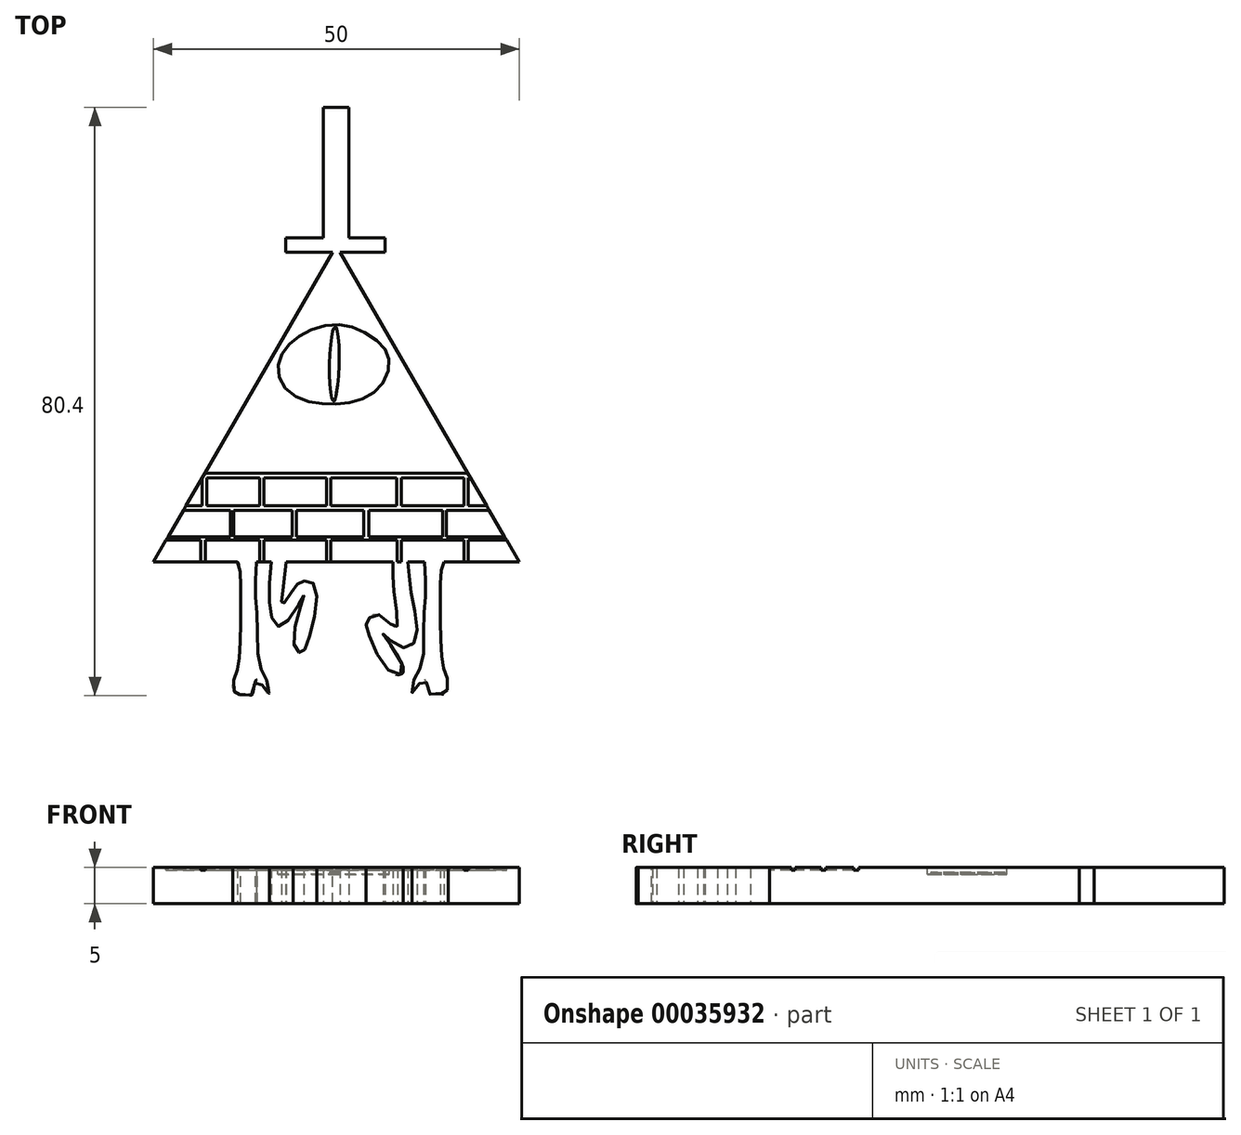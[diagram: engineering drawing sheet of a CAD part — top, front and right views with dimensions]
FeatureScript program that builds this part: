
annotation { "Feature Type Name" : "Feature", "Feature Type Description" : "" }
export const myFeature = defineFeature(function(context is Context, id is Id, definition is map)
    precondition{}
    {
        {
            var Q0;
            Q0=qCreatedBy(makeId("Top.planeOp"),FACE);
            var sketch = newSketch(context, id + "F0", { "sketchPlane" : qUnion([Q0])});
            skLineSegment(sketch, "E0", {"start": v(0, 43.3) * mm, "end": v(-25, 0) * mm});
            skLineSegment(sketch, "E1", {"start": v(-25, 0) * mm, "end": v(25, 0) * mm});
            skLineSegment(sketch, "E2", {"start": v(25, 0) * mm, "end": v(0, 43.3) * mm});
            skLineSegment(sketch, "E3.bottom", {"start": v(-6.91, 44.37) * mm, "end": v(6.68, 44.37) * mm});
            skLineSegment(sketch, "E3.top", {"start": v(-6.91, 42.4) * mm, "end": v(6.68, 42.4) * mm});
            skLineSegment(sketch, "E3.left", {"start": v(-6.91, 44.37) * mm, "end": v(-6.91, 42.4) * mm});
            skLineSegment(sketch, "E3.right", {"start": v(6.68, 44.37) * mm, "end": v(6.68, 42.4) * mm});
            skLineSegment(sketch, "E4.bottom", {"start": v(-1.76, 62.16) * mm, "end": v(1.7, 62.16) * mm});
            skLineSegment(sketch, "E4.top", {"start": v(-1.76, 42.4) * mm, "end": v(1.7, 42.4) * mm});
            skLineSegment(sketch, "E4.left", {"start": v(-1.76, 62.16) * mm, "end": v(-1.76, 42.4) * mm});
            skLineSegment(sketch, "E4.right", {"start": v(1.7, 62.16) * mm, "end": v(1.7, 42.4) * mm});
            skFitSpline(sketch, "E5", {"points": [v(-8.9, 0) * mm, v(-8.8, -7.65) * mm, v(-7.35, -8.7) * mm, v(-4.44, -4.65) * mm, v(-5.9, -10.56) * mm, v(-4.86, -12.43) * mm, v(-3.82, -10.66) * mm, v(-2.99, -3.09) * mm, v(-4.75, -2.67) * mm, v(-5.69, -3.5) * mm, v(-7.35, -5.79) * mm, v(-6.83, 0) * mm], "startDerivative": vector(-6.57, -68.42) * mm, "endDerivative": vector(6.6, 85.35) * mm});
            skFitSpline(sketch, "E6", {"points": [v(7.74, 0) * mm, v(7.95, -4.5) * mm, v(8.14, -8.99) * mm, v(5.66, -7.15) * mm, v(4.23, -8.08) * mm, v(4.23, -9.3) * mm, v(7.54, -15.12) * mm, v(9.17, -14.8) * mm, v(6.4, -9.85) * mm, v(8.68, -11.58) * mm, v(10.84, -10.66) * mm, v(10.34, -4.69) * mm, v(9.8, 0) * mm], "startDerivative": vector(0.32, -42.65) * mm, "endDerivative": vector(-4.02, 37.85) * mm});
            skFitSpline(sketch, "E7.MirrorCS", {"points": [v(12.07, 0.02) * mm, v(12.2, -4.33) * mm, v(11.94, -8.38) * mm, v(11.68, -14) * mm, v(10.63, -16.08) * mm, v(10.46, -17.9) * mm, v(12.03, -15.96) * mm, v(12.73, -18.06) * mm, v(13.26, -17.94) * mm, v(13.7, -18.05) * mm, v(14.2, -17.94) * mm, v(14.6, -18.1) * mm, v(15.3, -17) * mm, v(14.9, -15.24) * mm, v(14.5, -13.53) * mm, v(14.25, -9.74) * mm, v(14.25, -4.51) * mm, v(14.34, -1.18) * mm, v(14.7, -0.1) * mm, v(14.95, 0.02) * mm], "startDerivative": vector(3.73, -56.97) * mm, "endDerivative": vector(17.24, -25.07) * mm});
            skFitSpline(sketch, "E8", {"points": [v(-10.9, 0.02) * mm, v(-11.04, -4.46) * mm, v(-10.78, -8.52) * mm, v(-10.52, -14.14) * mm, v(-9.47, -16.22) * mm, v(-9.3, -18.03) * mm, v(-10.87, -16.1) * mm, v(-11.57, -18.2) * mm, v(-12.1, -18.07) * mm, v(-12.53, -18.18) * mm, v(-13.03, -18.07) * mm, v(-13.45, -18.24) * mm, v(-14.14, -17.14) * mm, v(-13.74, -15.38) * mm, v(-13.34, -13.67) * mm, v(-13.09, -9.88) * mm, v(-13.09, -4.65) * mm, v(-13.17, -1.31) * mm, v(-13.52, 0.02) * mm, v(-13.78, 0.02) * mm], "startDerivative": vector(-3.7, -61.3) * mm, "endDerivative": vector(-17.65, -5.45) * mm});
            skSolve(sketch);
        }
        {
            var Q0;
            Q0 = qSketchRegion(id + "F0", true);
            extrude(context, id + "F1", {"entities" : qUnion([Q0]), "depth" : 5 * mm});
        }
        {
            var Q0;
            Q0=makeQuery(id+"F1.opExtrude","CAP_FACE",FACE,{"disambiguationData":[OSD([sQuery(id+"F0.wireOp",EDGE,"E1"),sQuery(id+"F0.wireOp",EDGE,"E3.bottom"),sQuery(id+"F0.wireOp",EDGE,"E3.top"),sQuery(id+"F0.wireOp",EDGE,"E3.left"),sQuery(id+"F0.wireOp",EDGE,"E3.right"),sQuery(id+"F0.wireOp",EDGE,"E4.bottom"),sQuery(id+"F0.wireOp",EDGE,"E4.top"),sQuery(id+"F0.wireOp",EDGE,"E4.left"),sQuery(id+"F0.wireOp",EDGE,"E4.right"),sQuery(id+"F0.wireOp",EDGE,"E5"),sQuery(id+"F0.wireOp",EDGE,"E6"),sQuery(id+"F0.wireOp",EDGE,"E7.MirrorCS"),sQuery(id+"F0.wireOp",EDGE,"E8"),sQuery(id+"F0.wireOp",EDGE,"E0"),sQuery(id+"F0.wireOp",EDGE,"E2")])],"isStart":false});
            var sketch = newSketch(context, id + "F2", { "sketchPlane" : qUnion([Q0])});
            skFitSpline(sketch, "E9", {"points": [v(-7.95, 26.97) * mm, v(-6.71, 29.45) * mm, v(-4.03, 31.52) * mm, v(-0.1, 32.45) * mm, v(3.43, 31.63) * mm, v(6.45, 29.42) * mm, v(7.24, 27.28) * mm, v(6.14, 24.16) * mm, v(3.23, 22.18) * mm, v(-0.4, 21.62) * mm, v(-4.08, 22.04) * mm, v(-7.17, 24.05) * mm, v(-7.95, 26.97) * mm]});
            skSolve(sketch);
        }
        {
            var Q0;
            Q0=makeQuery(id+"F2.imprint","IMPRINT",FACE,{"disambiguationData":[TD([[makeQuery(id+"F2.imprint","IMPRINT",EDGE,{"derivedFrom":sQuery(id+"F2.wireOp",EDGE,"E9")}),-1.0]])]});
            extrude(context, id + "F3", {"entities" : qUnion([Q0]), "operationType" : NewBodyOperationType.REMOVE, "oppositeDirection" : true, "depth" : 1 * mm});
        }
        {
            var Q0;
            Q0=makeQuery(id+"F3.boolean.opBoolean","COPY",FACE,{"derivedFrom":makeQuery(id+"F3.opExtrude","CAP_FACE",FACE,{"disambiguationData":[OSD([sQuery(id+"F2.wireOp",EDGE,"E9")])],"isStart":false})});
            var sketch = newSketch(context, id + "F4", { "sketchPlane" : qUnion([Q0])});
            skFitSpline(sketch, "E10", {"points": [v(-0.15, 32.17) * mm, v(-0.02, 32.12) * mm, v(0.4, 28.1) * mm, v(-0.2, 22.18) * mm, v(-0.35, 22.04) * mm, v(-0.54, 22.16) * mm, v(-0.9, 28.03) * mm, v(-0.3, 32.05) * mm, v(-0.15, 32.17) * mm]});
            skSolve(sketch);
        }
        {
            var Q0;
            Q0 = qSketchRegion(id + "F4", true);
            extrude(context, id + "F5", {"entities" : qUnion([Q0]), "depth" : 0.3 * mm});
        }
        {
            var Q0;
            Q0=makeQuery(id+"F1.opExtrude","CAP_FACE",FACE,{"disambiguationData":[OSD([sQuery(id+"F0.wireOp",EDGE,"E1"),sQuery(id+"F0.wireOp",EDGE,"E3.bottom"),sQuery(id+"F0.wireOp",EDGE,"E3.top"),sQuery(id+"F0.wireOp",EDGE,"E3.left"),sQuery(id+"F0.wireOp",EDGE,"E3.right"),sQuery(id+"F0.wireOp",EDGE,"E4.bottom"),sQuery(id+"F0.wireOp",EDGE,"E4.top"),sQuery(id+"F0.wireOp",EDGE,"E4.left"),sQuery(id+"F0.wireOp",EDGE,"E4.right"),sQuery(id+"F0.wireOp",EDGE,"E5"),sQuery(id+"F0.wireOp",EDGE,"E6"),sQuery(id+"F0.wireOp",EDGE,"E7.MirrorCS"),sQuery(id+"F0.wireOp",EDGE,"E8"),sQuery(id+"F0.wireOp",EDGE,"E0"),sQuery(id+"F0.wireOp",EDGE,"E2")])],"isStart":false});
            var sketch = newSketch(context, id + "F6", { "sketchPlane" : qUnion([Q0])});
            skLineSegment(sketch, "E11", {"start": v(-23.28, 2.98) * mm, "end": v(23.28, 2.98) * mm});
            skLineSegment(sketch, "E12", {"start": v(23, 3.47) * mm, "end": v(-23, 3.47) * mm});
            skLineSegment(sketch, "E13", {"start": v(-20.92, 7.06) * mm, "end": v(20.92, 7.06) * mm});
            skLineSegment(sketch, "E14", {"start": v(20.55, 7.7) * mm, "end": v(-20.55, 7.7) * mm});
            skLineSegment(sketch, "E15", {"start": v(-18.36, 11.5) * mm, "end": v(18.36, 11.5) * mm});
            skLineSegment(sketch, "E16", {"start": v(17.98, 12.17) * mm, "end": v(-17.97, 12.17) * mm});
            skLineSegment(sketch, "E17", {"start": v(-17.97, 12.17) * mm, "end": v(-18.36, 11.5) * mm});
            skLineSegment(sketch, "E18", {"start": v(18.36, 11.5) * mm, "end": v(17.98, 12.17) * mm});
            skLineSegment(sketch, "E19", {"start": v(20.92, 7.06) * mm, "end": v(20.55, 7.7) * mm});
            skLineSegment(sketch, "E20", {"start": v(23.28, 2.98) * mm, "end": v(23, 3.47) * mm});
            skLineSegment(sketch, "E21", {"start": v(-20.55, 7.7) * mm, "end": v(-20.92, 7.06) * mm});
            skLineSegment(sketch, "E22", {"start": v(-23, 3.47) * mm, "end": v(-23.28, 2.98) * mm});
            skLineSegment(sketch, "E23", {"start": v(-17.92, 2.98) * mm, "end": v(-17.92, 0) * mm});
            skLineSegment(sketch, "E24", {"start": v(-18.54, 2.98) * mm, "end": v(-18.54, 0) * mm});
            skLineSegment(sketch, "E25", {"start": v(-17.92, 0) * mm, "end": v(-18.54, 0) * mm});
            skLineSegment(sketch, "E26", {"start": v(-18.36, 11.5) * mm, "end": v(-18.36, 7.7) * mm});
            skLineSegment(sketch, "E27", {"start": v(-18.36, 11.5) * mm, "end": v(-17.72, 12.6) * mm});
            skLineSegment(sketch, "E28", {"start": v(-14.5, 7.06) * mm, "end": v(-14.5, 3.47) * mm});
            skLineSegment(sketch, "E29", {"start": v(-14.06, 3.47) * mm, "end": v(-14.06, 7.06) * mm});
            skLineSegment(sketch, "E30", {"start": v(-17.72, 11.5) * mm, "end": v(-17.72, 7.7) * mm});
            skLineSegment(sketch, "E31", {"start": v(-10.45, 2.98) * mm, "end": v(-10.45, 0) * mm});
            skLineSegment(sketch, "E32", {"start": v(-9.9, 0) * mm, "end": v(-9.9, 2.98) * mm});
            skLineSegment(sketch, "E33", {"start": v(-9.9, 7.7) * mm, "end": v(-9.9, 11.5) * mm});
            skLineSegment(sketch, "E34", {"start": v(-10.45, 7.7) * mm, "end": v(-10.45, 11.5) * mm});
            skLineSegment(sketch, "E35", {"start": v(-6.05, 7.06) * mm, "end": v(-6.05, 3.47) * mm});
            skLineSegment(sketch, "E36", {"start": v(-5.46, 7.06) * mm, "end": v(-5.46, 3.47) * mm});
            skLineSegment(sketch, "E37", {"start": v(-1.32, 11.5) * mm, "end": v(-1.32, 7.7) * mm});
            skLineSegment(sketch, "E38", {"start": v(-0.76, 11.5) * mm, "end": v(-0.76, 7.7) * mm});
            skLineSegment(sketch, "E39", {"start": v(-0.76, 2.98) * mm, "end": v(-0.76, 0) * mm});
            skLineSegment(sketch, "E40", {"start": v(-1.32, 2.98) * mm, "end": v(-1.32, 0) * mm});
            skLineSegment(sketch, "E41", {"start": v(3.74, 7.06) * mm, "end": v(3.74, 3.47) * mm});
            skLineSegment(sketch, "E42", {"start": v(4.46, 7.06) * mm, "end": v(4.46, 3.47) * mm});
            skLineSegment(sketch, "E43", {"start": v(8.33, 11.5) * mm, "end": v(8.33, 7.7) * mm});
            skLineSegment(sketch, "E44", {"start": v(8.89, 11.5) * mm, "end": v(8.89, 7.7) * mm});
            skLineSegment(sketch, "E45", {"start": v(8.89, 2.98) * mm, "end": v(8.89, 0) * mm});
            skLineSegment(sketch, "E46", {"start": v(8.33, 2.98) * mm, "end": v(8.33, 0) * mm});
            skLineSegment(sketch, "E47", {"start": v(14.55, 7.06) * mm, "end": v(14.55, 3.47) * mm});
            skLineSegment(sketch, "E48", {"start": v(15.03, 7.06) * mm, "end": v(15.03, 3.47) * mm});
            skLineSegment(sketch, "E49", {"start": v(17.46, 11.5) * mm, "end": v(17.46, 7.7) * mm});
            skLineSegment(sketch, "E50", {"start": v(18.02, 11.5) * mm, "end": v(18.02, 7.7) * mm});
            skLineSegment(sketch, "E51", {"start": v(18.02, 2.98) * mm, "end": v(18.02, 0) * mm});
            skLineSegment(sketch, "E52", {"start": v(17.46, 2.98) * mm, "end": v(17.46, 0) * mm});
            skSolve(sketch);
        }
        {
            var Q0;
            Q0 = qSketchRegion(id + "F6", true);
            extrude(context, id + "F7", {"entities" : qUnion([Q0]), "operationType" : NewBodyOperationType.REMOVE, "oppositeDirection" : true, "depth" : 0.4 * mm});
        }
        {
            var Q0;
            {var subQ1=sQuery(id+"F6.wireOp",EDGE,"E30");Q0=makeQuery(id+"F7.boolean.opBoolean","SPLIT",FACE,{"disambiguationData":[TD([makeQuery(id+"F7.opExtrude","SWEPT_FACE",FACE,{"disambiguationData":[OSD([subQ1])]})])],"derivedFrom":makeQuery(id+"F1.opExtrude","CAP_FACE",FACE,{"disambiguationData":[OSD([sQuery(id+"F0.wireOp",EDGE,"E1"),sQuery(id+"F0.wireOp",EDGE,"E3.bottom"),sQuery(id+"F0.wireOp",EDGE,"E3.top"),sQuery(id+"F0.wireOp",EDGE,"E3.left"),sQuery(id+"F0.wireOp",EDGE,"E3.right"),sQuery(id+"F0.wireOp",EDGE,"E4.bottom"),sQuery(id+"F0.wireOp",EDGE,"E4.top"),sQuery(id+"F0.wireOp",EDGE,"E4.left"),sQuery(id+"F0.wireOp",EDGE,"E4.right"),sQuery(id+"F0.wireOp",EDGE,"E5"),sQuery(id+"F0.wireOp",EDGE,"E6"),sQuery(id+"F0.wireOp",EDGE,"E7.MirrorCS"),sQuery(id+"F0.wireOp",EDGE,"E8"),sQuery(id+"F0.wireOp",EDGE,"E0"),sQuery(id+"F0.wireOp",EDGE,"E2")])],"isStart":false})});}
            var sketch = newSketch(context, id + "F8", { "sketchPlane" : qUnion([Q0])});
            skLineSegment(sketch, "E53.bottom", {"start": v(-10.46, 11.5) * mm, "end": v(-9.93, 11.5) * mm});
            skLineSegment(sketch, "E53.top", {"start": v(-10.46, 7.7) * mm, "end": v(-9.93, 7.7) * mm});
            skLineSegment(sketch, "E53.left", {"start": v(-10.46, 11.5) * mm, "end": v(-10.46, 7.7) * mm});
            skLineSegment(sketch, "E53.right", {"start": v(-9.93, 11.5) * mm, "end": v(-9.93, 7.7) * mm});
            skLineSegment(sketch, "E54.bottom", {"start": v(-1.33, 11.5) * mm, "end": v(-0.73, 11.5) * mm});
            skLineSegment(sketch, "E54.top", {"start": v(-1.33, 7.7) * mm, "end": v(-0.73, 7.7) * mm});
            skLineSegment(sketch, "E54.left", {"start": v(-1.33, 11.5) * mm, "end": v(-1.33, 7.7) * mm});
            skLineSegment(sketch, "E54.right", {"start": v(-0.73, 11.5) * mm, "end": v(-0.73, 7.7) * mm});
            skLineSegment(sketch, "E55.bottom", {"start": v(-6.05, 7.06) * mm, "end": v(-5.47, 7.06) * mm});
            skLineSegment(sketch, "E55.top", {"start": v(-6.05, 3.47) * mm, "end": v(-5.47, 3.47) * mm});
            skLineSegment(sketch, "E55.left", {"start": v(-6.05, 7.06) * mm, "end": v(-6.05, 3.47) * mm});
            skLineSegment(sketch, "E55.right", {"start": v(-5.47, 7.06) * mm, "end": v(-5.47, 3.47) * mm});
            skLineSegment(sketch, "E56.bottom", {"start": v(-10.46, 3.03) * mm, "end": v(-9.93, 3.03) * mm});
            skLineSegment(sketch, "E56.top", {"start": v(-10.46, 0) * mm, "end": v(-9.93, 0) * mm});
            skLineSegment(sketch, "E56.left", {"start": v(-10.46, 3.03) * mm, "end": v(-10.46, 0) * mm});
            skLineSegment(sketch, "E56.right", {"start": v(-9.93, 3.03) * mm, "end": v(-9.93, 0) * mm});
            skLineSegment(sketch, "E57.bottom", {"start": v(-1.31, 3.02) * mm, "end": v(-0.74, 3.02) * mm});
            skLineSegment(sketch, "E57.top", {"start": v(-1.31, 0.02) * mm, "end": v(-0.74, 0.02) * mm});
            skLineSegment(sketch, "E57.left", {"start": v(-1.31, 3.02) * mm, "end": v(-1.31, 0.02) * mm});
            skLineSegment(sketch, "E57.right", {"start": v(-0.74, 3.02) * mm, "end": v(-0.74, 0.02) * mm});
            skLineSegment(sketch, "E58.bottom", {"start": v(8.33, 3.03) * mm, "end": v(8.92, 3.03) * mm});
            skLineSegment(sketch, "E58.top", {"start": v(8.33, 0.03) * mm, "end": v(8.92, 0.03) * mm});
            skLineSegment(sketch, "E58.left", {"start": v(8.33, 3.03) * mm, "end": v(8.33, 0.03) * mm});
            skLineSegment(sketch, "E58.right", {"start": v(8.92, 3.03) * mm, "end": v(8.92, 0.03) * mm});
            skLineSegment(sketch, "E59.bottom", {"start": v(17.45, 3.02) * mm, "end": v(18.05, 3.02) * mm});
            skLineSegment(sketch, "E59.top", {"start": v(17.45, -0.02) * mm, "end": v(18.05, -0.02) * mm});
            skLineSegment(sketch, "E59.left", {"start": v(17.45, 3.02) * mm, "end": v(17.45, -0.02) * mm});
            skLineSegment(sketch, "E59.right", {"start": v(18.05, 3.02) * mm, "end": v(18.05, -0.02) * mm});
            skLineSegment(sketch, "E60.bottom", {"start": v(3.75, 7.16) * mm, "end": v(4.46, 7.16) * mm});
            skLineSegment(sketch, "E60.top", {"start": v(3.75, 3.3) * mm, "end": v(4.46, 3.3) * mm});
            skLineSegment(sketch, "E60.left", {"start": v(3.75, 7.16) * mm, "end": v(3.75, 3.3) * mm});
            skLineSegment(sketch, "E60.right", {"start": v(4.46, 7.16) * mm, "end": v(4.46, 3.3) * mm});
            skLineSegment(sketch, "E61.bottom", {"start": v(8.28, 11.8) * mm, "end": v(8.9, 11.8) * mm});
            skLineSegment(sketch, "E61.top", {"start": v(8.28, 7.56) * mm, "end": v(8.9, 7.56) * mm});
            skLineSegment(sketch, "E61.left", {"start": v(8.28, 11.8) * mm, "end": v(8.28, 7.56) * mm});
            skLineSegment(sketch, "E61.right", {"start": v(8.9, 11.8) * mm, "end": v(8.9, 7.56) * mm});
            skSolve(sketch);
        }
        {
            var Q0;
            Q0 = qSketchRegion(id + "F8", true);
            extrude(context, id + "F9", {"entities" : qUnion([Q0]), "operationType" : NewBodyOperationType.REMOVE, "oppositeDirection" : true, "depth" : .4 * mm});
        }
    });
